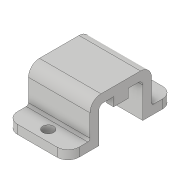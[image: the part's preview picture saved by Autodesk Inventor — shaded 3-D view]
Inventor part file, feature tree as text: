
AUTODESK INVENTOR PART (.ipt)
format: ipt  version: 2017 (Build 210142000, 142)  size: 154,112 bytes
history: native  units: in
note: dims shown in document units (in); Inventor stores cm internally (conversion verified against a paired STEP export)
features: fillet x4, extrude x3, sketch x3
ambient origin geometry x8: Origin, YZ Plane, XZ Plane, XY Plane, X Axis, Y Axis, Z Axis, Center Point
bodies: Solid1 (feature_tree)
feature tree (10):
  extrude  "Extrusion1"  Depth=0.4in
  extrude  "Extrusion2"  Depth=0.7in
  fillet  "Fillet1"  Radius=0.1in
  fillet  "Fillet2"  Radius=0.25in
  sketch  "Sketch3"  dims[d7=0.35in d8=0.35in d9=0.7in d10=0.0in d11=0.08in d12=0.0in d13=0.166in d14=0.166in d15=0.1in d16=0.0in d17=0.05in d18=0.125in d19=0.125in d20=0.125in d21=0.35in d22=0.35in d23=0.125in d24=0.125in d25=0.125in d26=0.275in d27=0.0in d28=0.025in]
  fillet  "Fillet3"  Radius=0.1in
  extrude  "Extrusion3"  Depth=0.35in
  fillet  "Fillet4"  Radius=0.7in
  sketch  "Sketch1"  dims[d0=0.5in d1=0.4in]
  sketch  "Sketch2"  dims[d2=0.5in d3=0.7in d4=0.1in d5=0.25in d6=0.1in]
